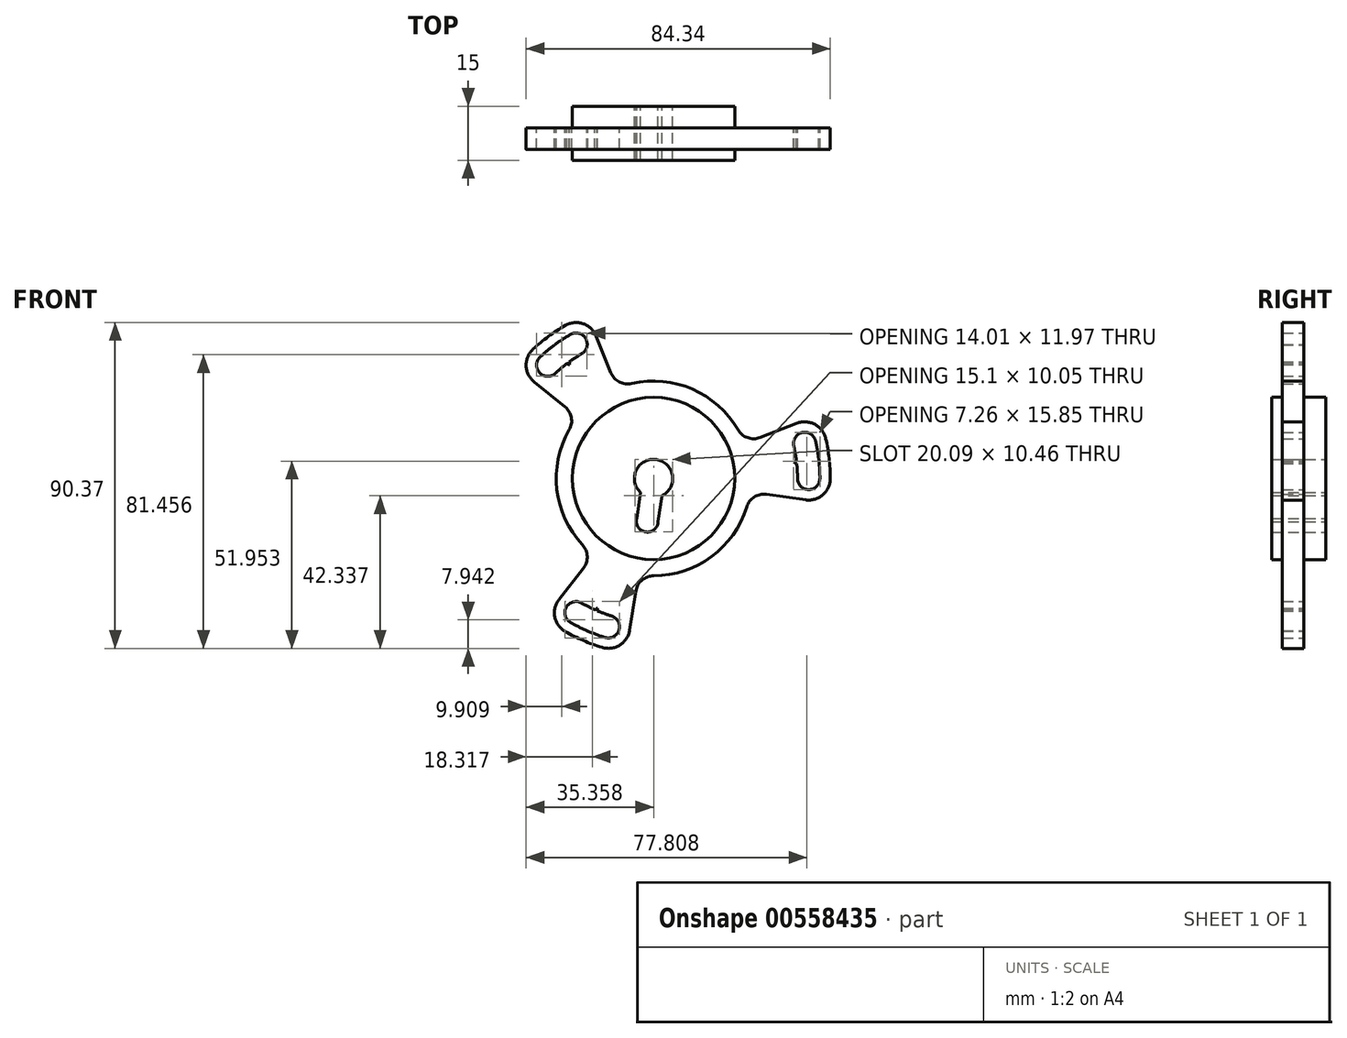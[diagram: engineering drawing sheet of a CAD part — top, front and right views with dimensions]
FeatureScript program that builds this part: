
annotation { "Feature Type Name" : "Feature", "Feature Type Description" : "" }
export const myFeature = defineFeature(function(context is Context, id is Id, definition is map)
    precondition{}
    {
        {
            var Q0;
            Q0=qCreatedBy(makeId("Front.planeOp"),FACE);
            var sketch = newSketch(context, id + "F0", { "sketchPlane" : qUnion([Q0])});
            skArc(sketch, "E0", {"start": v(-24.5, 42.44) * mm, "mid": v(-29.15, 39.38) * mm, "end": v(-33.43, 35.82) * mm});
            skArc(sketch, "E1", {"start": v(4.4, 2.98) * mm, "mid": v(3.36, 4.11) * mm, "end": v(2.04, 4.9) * mm});
            skArc(sketch, "E2", {"start": v(-19.95, 34.55) * mm, "mid": v(-18.82, 38.79) * mm, "end": v(-23.05, 39.92) * mm});
            skLineSegment(sketch, "E3.MirrorCS", {"start": v(-3.1, -4.3) * mm, "end": v(-3.68, -4.52) * mm});
            skArc(sketch, "E4.trimOffspring", {"start": v(2.31, -4.78) * mm, "mid": v(3.47, -4.02) * mm, "end": v(4.4, -2.98) * mm});
            skLineSegment(sketch, "E5.MirrorCS", {"start": v(2.31, -4.78) * mm, "end": v(1.24, -12.01) * mm});
            skArc(sketch, "E6.MirrorCS", {"start": v(-3.6, -3.9) * mm, "mid": v(-5.3, -0.15) * mm, "end": v(-3.8, 3.7) * mm});
            skLineSegment(sketch, "E7.MirrorCS", {"start": v(-3.6, -3.9) * mm, "end": v(-4.66, -11.13) * mm});
            skArc(sketch, "E8.MirrorCS", {"start": v(-4.66, -11.13) * mm, "mid": v(-2.2, -14.84) * mm, "end": v(1.24, -12.01) * mm});
            skArc(sketch, "E9.MirrorCS", {"start": v(2.04, 4.9) * mm, "mid": v(5.3, 0.15) * mm, "end": v(2.31, -4.78) * mm});
            skArc(sketch, "E10.trimOffspring", {"start": v(-3.8, 3.7) * mm, "mid": v(-4.64, 2.6) * mm, "end": v(-5.15, 1.3) * mm});
            skArc(sketch, "E11", {"start": v(2.31, -4.78) * mm, "mid": v(0.46, 5.29) * mm, "end": v(-3.1, -4.3) * mm});
            skArc(sketch, "E12.MirrorC", {"start": v(-27.22, 29.17) * mm, "mid": v(-31.6, 29.32) * mm, "end": v(-31.45, 33.7) * mm});
            skArc(sketch, "E13", {"start": v(-19.95, 34.55) * mm, "mid": v(-23.74, 32.07) * mm, "end": v(-27.22, 29.17) * mm});
            skArc(sketch, "E14", {"start": v(-23.05, 39.92) * mm, "mid": v(-27.43, 37.05) * mm, "end": v(-31.45, 33.7) * mm});
            skArc(sketch, "E15", {"start": v(-23.39, 13.49) * mm, "mid": v(-26.83, -3.06) * mm, "end": v(-19.75, -18.41) * mm});
            skArc(sketch, "E16", {"start": v(-33.43, 35.82) * mm, "mid": v(-35.33, 31.23) * mm, "end": v(-33.1, 26.77) * mm});
            skArc(sketch, "E17", {"start": v(-27.5, 37.15) * mm, "mid": v(-27.5, 37.08) * mm, "end": v(-27.5, 37) * mm});
            skArc(sketch, "E18.trimOffspring", {"start": v(-24.07, 31.82) * mm, "mid": v(-23.71, 31.66) * mm, "end": v(-23.34, 31.53) * mm});
            skArc(sketch, "E19.trimOffspring", {"start": v(-27.36, 37.1) * mm, "mid": v(-27.43, 37.13) * mm, "end": v(-27.5, 37.15) * mm});
            skLineSegment(sketch, "E20", {"start": v(-21, 16.98) * mm, "end": v(-33.1, 26.77) * mm});
            skLineSegment(sketch, "E21", {"start": v(-33.1, 26.77) * mm, "end": v(-24.58, 19.87) * mm});
            skArc(sketch, "E22.trimOffspring", {"start": v(-23.34, 31.53) * mm, "mid": v(-23.36, 31.92) * mm, "end": v(-23.4, 32.32) * mm});
            skArc(sketch, "E23.trimOffspring", {"start": v(-15.94, 39.48) * mm, "mid": v(-19.55, 42.91) * mm, "end": v(-24.5, 42.44) * mm});
            skLineSegment(sketch, "E24.trimOffspring", {"start": v(-11.83, 29.3) * mm, "end": v(-15.94, 39.48) * mm});
            skLineSegment(sketch, "E25.trimOffspring", {"start": v(-27.43, 37.05) * mm, "end": v(-27.5, 37.15) * mm});
            skLineSegment(sketch, "E26.MirrorCS", {"start": v(-18.37, -42.28) * mm, "end": v(-18.42, -42.39) * mm});
            skArc(sketch, "E27.MirrorCS", {"start": v(-18.3, -42.31) * mm, "mid": v(-18.36, -42.35) * mm, "end": v(-18.42, -42.39) * mm});
            skArc(sketch, "E28.MirrorCS", {"start": v(-18.42, -42.39) * mm, "mid": v(-18.44, -42.32) * mm, "end": v(-18.45, -42.25) * mm});
            skArc(sketch, "E29.MirrorCS", {"start": v(-16.29, -36.42) * mm, "mid": v(-15.97, -36.19) * mm, "end": v(-15.63, -35.97) * mm});
            skArc(sketch, "E30.MirrorCS", {"start": v(-15.63, -35.97) * mm, "mid": v(-15.56, -36.36) * mm, "end": v(-15.52, -36.76) * mm});
            skArc(sketch, "E31.MirrorCS", {"start": v(-13.46, -44.1) * mm, "mid": v(-18.37, -42.28) * mm, "end": v(-23.05, -39.92) * mm});
            skArc(sketch, "E32.MirrorCS", {"start": v(-11.65, -38.16) * mm, "mid": v(-15.9, -36.6) * mm, "end": v(-19.95, -34.55) * mm});
            skArc(sketch, "E33.MirrorCS", {"start": v(-11.65, -38.16) * mm, "mid": v(-9.6, -42.03) * mm, "end": v(-13.46, -44.1) * mm});
            skArc(sketch, "E34.MirrorCS", {"start": v(-14.3, -46.86) * mm, "mid": v(-19.53, -44.94) * mm, "end": v(-24.5, -42.44) * mm});
            skArc(sketch, "E35.MirrorCS", {"start": v(-6.63, -42.06) * mm, "mid": v(-9.38, -46.21) * mm, "end": v(-14.3, -46.86) * mm});
            skLineSegment(sketch, "E36.MirrorCS", {"start": v(-26.23, -33.54) * mm, "end": v(-19.47, -24.9) * mm});
            skArc(sketch, "E37.MirrorCS", {"start": v(-24.5, -42.44) * mm, "mid": v(-27.39, -38.38) * mm, "end": v(-26.23, -33.54) * mm});
            skLineSegment(sketch, "E38.MirrorCS", {"start": v(-4.92, -31.22) * mm, "end": v(-6.63, -42.06) * mm});
            skArc(sketch, "E39.MirrorCS", {"start": v(-19.95, -34.55) * mm, "mid": v(-24.18, -35.69) * mm, "end": v(-23.05, -39.92) * mm});
            skArc(sketch, "E40.trimOffspring", {"start": v(0.01, -27) * mm, "mid": v(16.06, -21.7) * mm, "end": v(25.82, -7.9) * mm});
            skLineSegment(sketch, "E41.MirrorCS", {"start": v(45.8, 5.23) * mm, "end": v(45.92, 5.24) * mm});
            skArc(sketch, "E42.MirrorCS", {"start": v(45.8, 5.31) * mm, "mid": v(45.86, 5.28) * mm, "end": v(45.92, 5.24) * mm});
            skArc(sketch, "E43.MirrorCS", {"start": v(45.92, 5.24) * mm, "mid": v(45.87, 5.2) * mm, "end": v(45.81, 5.14) * mm});
            skArc(sketch, "E44.MirrorCS", {"start": v(38.97, 4.45) * mm, "mid": v(39.27, 4.7) * mm, "end": v(39.6, 4.94) * mm});
            skArc(sketch, "E45.MirrorCS", {"start": v(39.69, 4.1) * mm, "mid": v(39.32, 4.27) * mm, "end": v(38.97, 4.45) * mm});
            skArc(sketch, "E46.MirrorCS", {"start": v(38.87, 8.99) * mm, "mid": v(39.64, 4.52) * mm, "end": v(39.9, 0) * mm});
            skArc(sketch, "E47.MirrorCS", {"start": v(44.91, 10.39) * mm, "mid": v(45.8, 5.23) * mm, "end": v(46.1, 0) * mm});
            skArc(sketch, "E48.MirrorCS", {"start": v(49, 0) * mm, "mid": v(46.94, -4.53) * mm, "end": v(42.16, -5.94) * mm});
            skArc(sketch, "E49.MirrorCS", {"start": v(39.74, 15.29) * mm, "mid": v(44.7, 14.99) * mm, "end": v(47.74, 11.04) * mm});
            skArc(sketch, "E50.MirrorCS", {"start": v(39.9, 0) * mm, "mid": v(43, -3.1) * mm, "end": v(46.1, 0) * mm});
            skArc(sketch, "E51.MirrorCS", {"start": v(47.74, 11.04) * mm, "mid": v(48.68, 5.56) * mm, "end": v(49, 0) * mm});
            skArc(sketch, "E52.MirrorCS", {"start": v(38.87, 8.99) * mm, "mid": v(41.2, 12.7) * mm, "end": v(44.91, 10.39) * mm});
            skLineSegment(sketch, "E53.MirrorCS", {"start": v(29.5, 11.35) * mm, "end": v(39.74, 15.29) * mm});
            skLineSegment(sketch, "E54.MirrorCS", {"start": v(42.16, -5.94) * mm, "end": v(31.3, -4.41) * mm});
            skArc(sketch, "E55.trimOffspring", {"start": v(23.38, 13.51) * mm, "mid": v(10.76, 24.76) * mm, "end": v(-6.07, 26.3) * mm});
            skPoint(sketch, "E56.visualSharp", {"position": v(25.2, 9.7) * mm});
            skArc(sketch, "E56.filletArc", {"start": v(23.38, 13.51) * mm, "mid": v(26.04, 11.3) * mm, "end": v(29.5, 11.35) * mm});
            skPoint(sketch, "E57.visualSharp", {"position": v(-10.1, 25.04) * mm});
            skArc(sketch, "E57.filletArc", {"start": v(-11.83, 29.3) * mm, "mid": v(-9.5, 26.75) * mm, "end": v(-6.07, 26.3) * mm});
            skPoint(sketch, "E58.visualSharp", {"position": v(-21, 16.98) * mm});
            skArc(sketch, "E58.filletArc", {"start": v(-23.39, 13.49) * mm, "mid": v(-22.8, 16.9) * mm, "end": v(-24.58, 19.87) * mm});
            skPoint(sketch, "E59.visualSharp", {"position": v(-16.63, -21.27) * mm});
            skArc(sketch, "E59.filletArc", {"start": v(-19.47, -24.9) * mm, "mid": v(-18.41, -21.6) * mm, "end": v(-19.75, -18.41) * mm});
            skPoint(sketch, "E60.visualSharp", {"position": v(-4.2, -26.67) * mm});
            skArc(sketch, "E60.filletArc", {"start": v(0.01, -27) * mm, "mid": v(-3.23, -28.2) * mm, "end": v(-4.92, -31.22) * mm});
            skPoint(sketch, "E61.visualSharp", {"position": v(26.74, -3.77) * mm});
            skArc(sketch, "E61.filletArc", {"start": v(31.3, -4.41) * mm, "mid": v(27.91, -5.14) * mm, "end": v(25.82, -7.9) * mm});
            skSolve(sketch);
        }
        {
            var Q0;
            Q0=makeQuery(id+"F0.imprint","IMPRINT",FACE,{"disambiguationData":[TD([[makeQuery(id+"F0.imprint","IMPRINT",EDGE,{"derivedFrom":sQuery(id+"F0.wireOp",EDGE,"E0")}),1.0]])]});
            extrude(context, id + "F1", {"entities" : qUnion([Q0]), "flatOperationType" : FlatOperationType.REMOVE, "depth" : 6 * mm, "offsetDistance" : 25 * mm, "domain" : OperationDomain.MODEL});
        }
        {
            var Q0;
            Q0=makeQuery(id+"F1.opExtrude","CAP_FACE",FACE,{"disambiguationData":[OSD([sQuery(id+"F0.wireOp",EDGE,"E0"),sQuery(id+"F0.wireOp",EDGE,"E1"),sQuery(id+"F0.wireOp",EDGE,"E2"),sQuery(id+"F0.wireOp",EDGE,"E4.trimOffspring"),sQuery(id+"F0.wireOp",EDGE,"E5.MirrorCS"),sQuery(id+"F0.wireOp",EDGE,"E6.MirrorCS"),sQuery(id+"F0.wireOp",EDGE,"E7.MirrorCS"),sQuery(id+"F0.wireOp",EDGE,"E8.MirrorCS"),sQuery(id+"F0.wireOp",EDGE,"E9.MirrorCS"),sQuery(id+"F0.wireOp",EDGE,"E11"),sQuery(id+"F0.wireOp",EDGE,"E12.MirrorC"),sQuery(id+"F0.wireOp",EDGE,"E13"),sQuery(id+"F0.wireOp",EDGE,"E14"),sQuery(id+"F0.wireOp",EDGE,"E15"),sQuery(id+"F0.wireOp",EDGE,"E16"),sQuery(id+"F0.wireOp",EDGE,"E17"),sQuery(id+"F0.wireOp",EDGE,"E18.trimOffspring"),sQuery(id+"F0.wireOp",EDGE,"E19.trimOffspring"),sQuery(id+"F0.wireOp",EDGE,"E20"),sQuery(id+"F0.wireOp",EDGE,"E22.trimOffspring"),sQuery(id+"F0.wireOp",EDGE,"E23.trimOffspring"),sQuery(id+"F0.wireOp",EDGE,"E24.trimOffspring"),sQuery(id+"F0.wireOp",EDGE,"E27.MirrorCS"),sQuery(id+"F0.wireOp",EDGE,"E28.MirrorCS"),sQuery(id+"F0.wireOp",EDGE,"E29.MirrorCS"),sQuery(id+"F0.wireOp",EDGE,"E30.MirrorCS"),sQuery(id+"F0.wireOp",EDGE,"E31.MirrorCS"),sQuery(id+"F0.wireOp",EDGE,"E32.MirrorCS"),sQuery(id+"F0.wireOp",EDGE,"E33.MirrorCS"),sQuery(id+"F0.wireOp",EDGE,"E34.MirrorCS"),sQuery(id+"F0.wireOp",EDGE,"E35.MirrorCS"),sQuery(id+"F0.wireOp",EDGE,"E36.MirrorCS"),sQuery(id+"F0.wireOp",EDGE,"E37.MirrorCS"),sQuery(id+"F0.wireOp",EDGE,"E38.MirrorCS"),sQuery(id+"F0.wireOp",EDGE,"E39.MirrorCS"),sQuery(id+"F0.wireOp",EDGE,"E40.trimOffspring"),sQuery(id+"F0.wireOp",EDGE,"E42.MirrorCS"),sQuery(id+"F0.wireOp",EDGE,"E43.MirrorCS"),sQuery(id+"F0.wireOp",EDGE,"E44.MirrorCS"),sQuery(id+"F0.wireOp",EDGE,"E45.MirrorCS"),sQuery(id+"F0.wireOp",EDGE,"E46.MirrorCS"),sQuery(id+"F0.wireOp",EDGE,"E47.MirrorCS"),sQuery(id+"F0.wireOp",EDGE,"E48.MirrorCS"),sQuery(id+"F0.wireOp",EDGE,"E49.MirrorCS"),sQuery(id+"F0.wireOp",EDGE,"E50.MirrorCS"),sQuery(id+"F0.wireOp",EDGE,"E51.MirrorCS"),sQuery(id+"F0.wireOp",EDGE,"E52.MirrorCS"),sQuery(id+"F0.wireOp",EDGE,"E53.MirrorCS"),sQuery(id+"F0.wireOp",EDGE,"E54.MirrorCS"),sQuery(id+"F0.wireOp",EDGE,"E55.trimOffspring"),sQuery(id+"F0.wireOp",EDGE,"E56.filletArc"),sQuery(id+"F0.wireOp",EDGE,"E57.filletArc"),sQuery(id+"F0.wireOp",EDGE,"E58.filletArc"),sQuery(id+"F0.wireOp",EDGE,"E59.filletArc"),sQuery(id+"F0.wireOp",EDGE,"E60.filletArc"),sQuery(id+"F0.wireOp",EDGE,"E61.filletArc")])],"isStart":false});
            var sketch = newSketch(context, id + "F2", { "sketchPlane" : qUnion([Q0])});
            skCircle(sketch, "E62", {"center": v(0, 0) * mm, "radius": 22.5 * mm});
            skSolve(sketch);
        }
        {
            var Q0;
            Q0=makeQuery(id+"F2.imprint","IMPRINT",FACE,{"disambiguationData":[TD([[makeQuery(id+"F2.imprint","IMPRINT",EDGE,{"derivedFrom":sQuery(id+"F2.wireOp",EDGE,"E62")}),1.0]])]});
            extrude(context, id + "F3", {"entities" : qUnion([Q0]), "operationType" : NewBodyOperationType.ADD, "depth" : 3 * mm, "offsetDistance" : 25 * mm, "hasSecondDirection" : true, "secondDirectionOppositeDirection" : true, "secondDirectionDepth" : 12 * mm});
        }
    });
